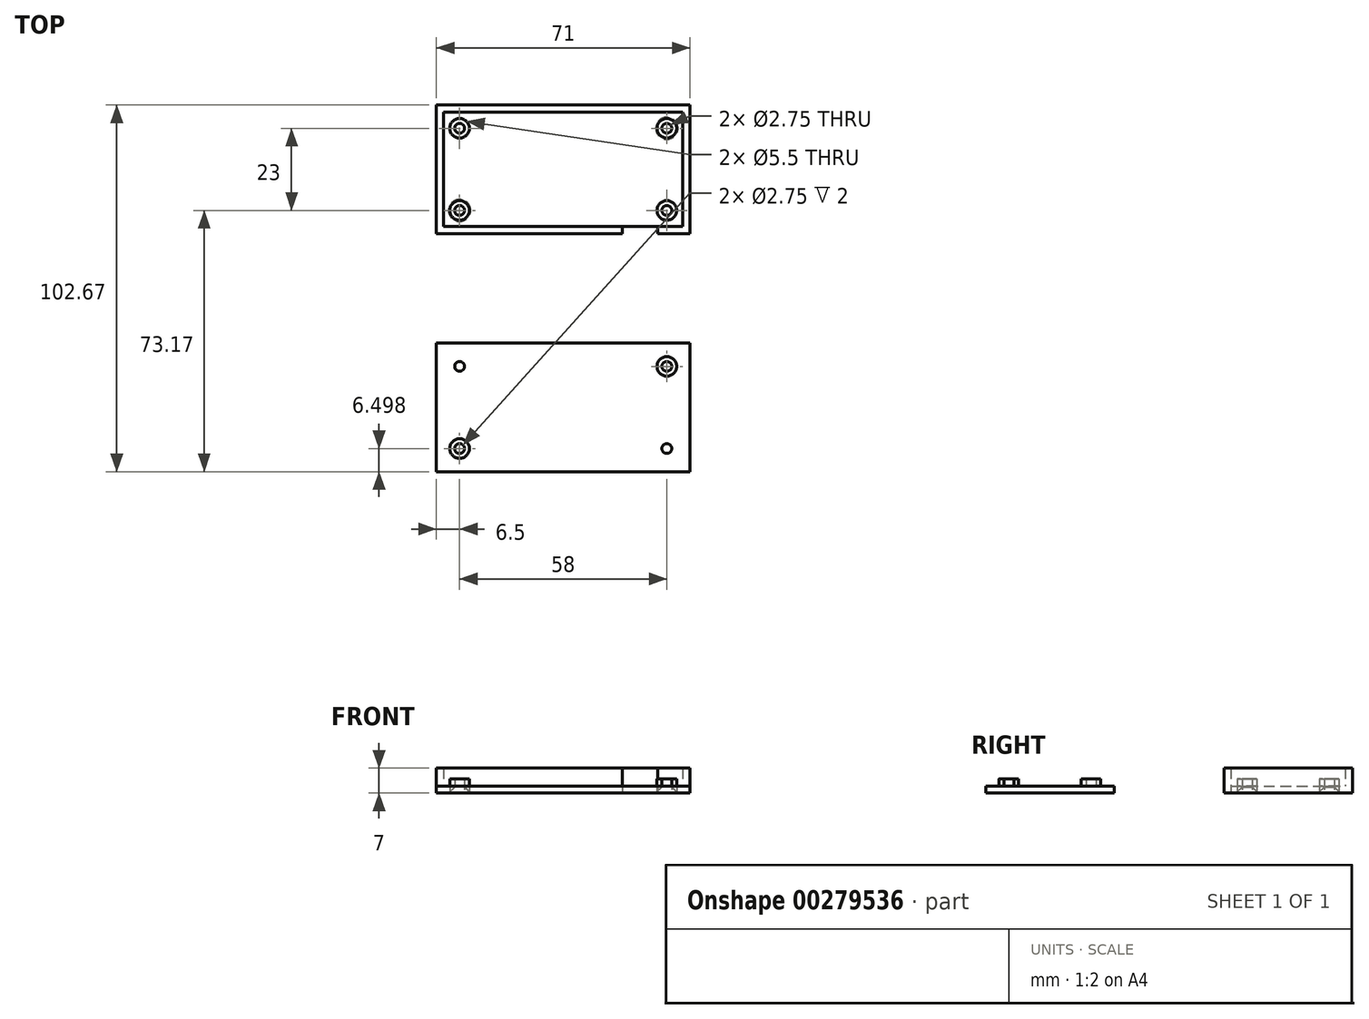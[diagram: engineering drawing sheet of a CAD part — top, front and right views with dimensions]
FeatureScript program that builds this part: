
annotation { "Feature Type Name" : "Feature", "Feature Type Description" : "" }
export const myFeature = defineFeature(function(context is Context, id is Id, definition is map)
    precondition{}
    {
        {
            var Q0;
            Q0=qCreatedBy(makeId("Top.planeOp"),FACE);
            var sketch = newSketch(context, id + "F0", { "sketchPlane" : qUnion([Q0])});
            skLineSegment(sketch, "E0.bottom", {"start": v(32.5, 15) * mm, "end": v(-32.5, 15) * mm});
            skLineSegment(sketch, "E0.top", {"start": v(32.5, -15) * mm, "end": v(-32.5, -15) * mm});
            skLineSegment(sketch, "E0.left", {"start": v(32.5, 15) * mm, "end": v(32.5, -15) * mm});
            skLineSegment(sketch, "E0.right", {"start": v(-32.5, 15) * mm, "end": v(-32.5, -15) * mm});
            skPoint(sketch, "E0.middle", {"position": v(0, 0) * mm});
            skCircle(sketch, "E1", {"center": v(29, 11.5) * mm, "radius": 1.38 * mm});
            skLineSegment(sketch, "E2", {"start": v(29, 15) * mm, "end": v(29, 11.5) * mm, "construction": true});
            skLineSegment(sketch, "E3", {"start": v(29, 11.5) * mm, "end": v(32.5, 11.5) * mm, "construction": true});
            skCircle(sketch, "E4.MirrorC", {"center": v(29, -11.5) * mm, "radius": 1.38 * mm});
            skCircle(sketch, "E5.MirrorC", {"center": v(-29, -11.5) * mm, "radius": 1.38 * mm});
            skCircle(sketch, "E6.MirrorC", {"center": v(-29, 11.5) * mm, "radius": 1.38 * mm});
            skLineSegment(sketch, "E7.0", {"start": v(33.5, 16) * mm, "end": v(-33.5, 16) * mm});
            skLineSegment(sketch, "E7.1", {"start": v(33.5, 16) * mm, "end": v(33.5, -16) * mm});
            skLineSegment(sketch, "E7.2", {"start": v(33.5, -16) * mm, "end": v(-33.5, -16) * mm});
            skLineSegment(sketch, "E7.3", {"start": v(-33.5, 16) * mm, "end": v(-33.5, -16) * mm});
            skLineSegment(sketch, "E8.0", {"start": v(35.5, 18) * mm, "end": v(-35.5, 18) * mm});
            skLineSegment(sketch, "E8.1", {"start": v(35.5, 18) * mm, "end": v(35.5, -18) * mm});
            skLineSegment(sketch, "E8.2", {"start": v(35.5, -18) * mm, "end": v(-35.5, -18) * mm});
            skLineSegment(sketch, "E8.3", {"start": v(-35.5, 18) * mm, "end": v(-35.5, -18) * mm});
            skLineSegment(sketch, "E9", {"start": v(-32.5, -15) * mm, "end": v(21.5, -15) * mm});
            skLineSegment(sketch, "E10.bottom", {"start": v(16.5, -15) * mm, "end": v(26.5, -15) * mm});
            skLineSegment(sketch, "E10.top", {"start": v(16.5, -18) * mm, "end": v(26.5, -18) * mm});
            skLineSegment(sketch, "E10.left", {"start": v(16.5, -15) * mm, "end": v(16.5, -18) * mm});
            skLineSegment(sketch, "E10.right", {"start": v(26.5, -15) * mm, "end": v(26.5, -18) * mm});
            skCircle(sketch, "E11", {"center": v(29, 11.5) * mm, "radius": 2.75 * mm});
            skCircle(sketch, "E12.MirrorC", {"center": v(29, -11.5) * mm, "radius": 2.75 * mm});
            skCircle(sketch, "E13.MirrorC", {"center": v(-29, -11.5) * mm, "radius": 2.75 * mm});
            skCircle(sketch, "E14.MirrorC", {"center": v(-29, 11.5) * mm, "radius": 2.75 * mm});
            skSolve(sketch);
        }
        {
            var Q0;
            Q0=makeQuery(id+"F0.imprint","IMPRINT",FACE,{"disambiguationData":[TD([[makeQuery(id+"F0.imprint","IMPRINT",EDGE,{"derivedFrom":sQuery(id+"F0.wireOp",EDGE,"E7.0")}),-1.0]])]});
            var Q1;
            Q1=makeQuery(id+"F0.imprint","IMPRINT",FACE,{"disambiguationData":[TD([[makeQuery(id+"F0.imprint","IMPRINT",EDGE,{"derivedFrom":sQuery(id+"F0.wireOp",EDGE,"E0.bottom")}),-1.0]])]});
            var Q2;
            Q2=makeQuery(id+"F0.imprint","IMPRINT",FACE,{"disambiguationData":[TD([[makeQuery(id+"F0.imprint","IMPRINT",EDGE,{"derivedFrom":sQuery(id+"F0.wireOp",EDGE,"E0.bottom")}),1.0]])]});
            var Q3;
            Q3=makeQuery(id+"F0.imprint","IMPRINT",FACE,{"disambiguationData":[TD([[makeQuery(id+"F0.imprint","IMPRINT",EDGE,{"derivedFrom":sQuery(id+"F0.wireOp",EDGE,"E6.MirrorC")}),1.0]])]});
            var Q4;
            Q4=makeQuery(id+"F0.imprint","IMPRINT",FACE,{"disambiguationData":[TD([[makeQuery(id+"F0.imprint","IMPRINT",EDGE,{"derivedFrom":sQuery(id+"F0.wireOp",EDGE,"E5.MirrorC")}),-1.0]])]});
            var Q5;
            Q5=makeQuery(id+"F0.imprint","IMPRINT",FACE,{"disambiguationData":[TD([[makeQuery(id+"F0.imprint","IMPRINT",EDGE,{"derivedFrom":sQuery(id+"F0.wireOp",EDGE,"E1")}),-1.0]])]});
            var Q6;
            Q6=makeQuery(id+"F0.imprint","IMPRINT",FACE,{"disambiguationData":[TD([[makeQuery(id+"F0.imprint","IMPRINT",EDGE,{"derivedFrom":sQuery(id+"F0.wireOp",EDGE,"E4.MirrorC")}),1.0]])]});
            var Q7;
            {var subQ5=sQuery(id+"F0.wireOp",EDGE,"E10.top");Q7=makeQuery(id+"F0.imprint","IMPRINT",FACE,{"disambiguationData":[TD([[makeQuery(id+"F0.imprint","IMPRINT",EDGE,{"derivedFrom":subQ5}),1.0]])]});}
            var Q8;
            {var subQ3=sQuery(id+"F0.wireOp",EDGE,"E7.2");var subQ5=sQuery(id+"F0.wireOp",EDGE,"E10.right");var subQ8=makeQuery(id+"F0.imprint","INTERSECT",VERTEX,{"derivedFrom":[subQ3,subQ5]});Q8=makeQuery(id+"F0.imprint","IMPRINT",FACE,{"disambiguationData":[TD([[makeQuery(id+"F0.imprint","IMPRINT",EDGE,{"disambiguationData":[TD([[subQ8,-1.0]])],"derivedFrom":subQ3}),-1.0]])]});}
            extrude(context, id + "F1", {"entities" : qUnion([Q0, Q1, Q2, Q3, Q4, Q5, Q6, Q7, Q8]), "depth" : 2 * mm});
        }
        {
            var Q0;
            Q0=makeQuery(id+"F0.imprint","IMPRINT",FACE,{"disambiguationData":[TD([[makeQuery(id+"F0.imprint","IMPRINT",EDGE,{"derivedFrom":sQuery(id+"F0.wireOp",EDGE,"E5.MirrorC")}),-1.0]])]});
            var Q1;
            Q1=makeQuery(id+"F0.imprint","IMPRINT",FACE,{"disambiguationData":[TD([[makeQuery(id+"F0.imprint","IMPRINT",EDGE,{"derivedFrom":sQuery(id+"F0.wireOp",EDGE,"E4.MirrorC")}),1.0]])]});
            var Q2;
            Q2=makeQuery(id+"F0.imprint","IMPRINT",FACE,{"disambiguationData":[TD([[makeQuery(id+"F0.imprint","IMPRINT",EDGE,{"derivedFrom":sQuery(id+"F0.wireOp",EDGE,"E1")}),-1.0]])]});
            var Q3;
            Q3=makeQuery(id+"F0.imprint","IMPRINT",FACE,{"disambiguationData":[TD([[makeQuery(id+"F0.imprint","IMPRINT",EDGE,{"derivedFrom":sQuery(id+"F0.wireOp",EDGE,"E6.MirrorC")}),1.0]])]});
            extrude(context, id + "F2", {"entities" : qUnion([Q0, Q1, Q2, Q3]), "operationType" : NewBodyOperationType.ADD, "depth" : 4 * mm});
        }
        {
            var Q0;
            Q0=makeQuery(id+"F0.imprint","IMPRINT",FACE,{"disambiguationData":[TD([[makeQuery(id+"F0.imprint","IMPRINT",EDGE,{"derivedFrom":sQuery(id+"F0.wireOp",EDGE,"E7.0")}),-1.0]])]});
            extrude(context, id + "F3", {"entities" : qUnion([Q0]), "operationType" : NewBodyOperationType.ADD, "depth" : 7 * mm});
        }
        {
            var Q0;
            Q0=makeQuery(id+"F1.opExtrude","CAP_EDGE",EDGE,{"disambiguationData":[OSD([sQuery(id+"F0.wireOp",EDGE,"E4.MirrorC")])],"isStart":true});
            var Q1;
            Q1=makeQuery(id+"F1.opExtrude","CAP_EDGE",EDGE,{"disambiguationData":[OSD([sQuery(id+"F0.wireOp",EDGE,"E1")])],"isStart":true});
            var Q2;
            Q2=makeQuery(id+"F1.opExtrude","CAP_EDGE",EDGE,{"disambiguationData":[OSD([sQuery(id+"F0.wireOp",EDGE,"E6.MirrorC")])],"isStart":true});
            var Q3;
            Q3=makeQuery(id+"F1.opExtrude","CAP_EDGE",EDGE,{"disambiguationData":[OSD([sQuery(id+"F0.wireOp",EDGE,"E5.MirrorC")])],"isStart":true});
            chamfer(context, id + "F4", {"entities" : qUnion([Q0, Q1, Q2, Q3]), "width" : 1.75 * mm, "tangentPropagation" : true});
        }
        {
            var Q0;
            Q0=qCreatedBy(makeId("Top.planeOp"),FACE);
            var sketch = newSketch(context, id + "F5", { "sketchPlane" : qUnion([Q0])});
            skLineSegment(sketch, "E15.bottom", {"start": v(35.5, -48.67) * mm, "end": v(-35.5, -48.67) * mm});
            skLineSegment(sketch, "E15.top", {"start": v(35.5, -84.67) * mm, "end": v(-35.5, -84.67) * mm});
            skLineSegment(sketch, "E15.left", {"start": v(35.5, -48.67) * mm, "end": v(35.5, -84.67) * mm});
            skLineSegment(sketch, "E15.right", {"start": v(-35.5, -48.67) * mm, "end": v(-35.5, -84.67) * mm});
            skPoint(sketch, "E15.middle", {"position": v(0, -66.67) * mm});
            skLineSegment(sketch, "E16", {"start": v(29, -48.67) * mm, "end": v(29, -55.17) * mm, "construction": true});
            skLineSegment(sketch, "E17", {"start": v(29, -55.17) * mm, "end": v(35.5, -55.17) * mm, "construction": true});
            skCircle(sketch, "E18", {"center": v(29, -55.17) * mm, "radius": 1.38 * mm});
            skCircle(sketch, "E19", {"center": v(29, -55.17) * mm, "radius": 2.75 * mm});
            skCircle(sketch, "E20.MirrorC", {"center": v(-29, -55.17) * mm, "radius": 1.38 * mm});
            skCircle(sketch, "E21.MirrorC", {"center": v(-29, -55.17) * mm, "radius": 2.75 * mm});
            skLineSegment(sketch, "E22", {"start": v(0, -66.67) * mm, "end": v(-17.15, -66.67) * mm});
            skCircle(sketch, "E23.MirrorC", {"center": v(29, -78.17) * mm, "radius": 1.38 * mm});
            skCircle(sketch, "E24.MirrorC", {"center": v(29, -78.17) * mm, "radius": 2.75 * mm});
            skCircle(sketch, "E25.MirrorC", {"center": v(-29, -78.17) * mm, "radius": 1.38 * mm});
            skCircle(sketch, "E26.MirrorC", {"center": v(-29, -78.17) * mm, "radius": 2.75 * mm});
            skSolve(sketch);
        }
        {
            var Q0;
            Q0=makeQuery(id+"F5.imprint","IMPRINT",FACE,{"disambiguationData":[TD([[makeQuery(id+"F5.imprint","IMPRINT",EDGE,{"derivedFrom":sQuery(id+"F5.wireOp",EDGE,"E15.bottom")}),1.0]])]});
            var Q1;
            Q1=makeQuery(id+"F5.imprint","IMPRINT",FACE,{"disambiguationData":[TD([[makeQuery(id+"F5.imprint","IMPRINT",EDGE,{"derivedFrom":sQuery(id+"F5.wireOp",EDGE,"E20.MirrorC")}),1.0]])]});
            var Q2;
            Q2=makeQuery(id+"F5.imprint","IMPRINT",FACE,{"disambiguationData":[TD([[makeQuery(id+"F5.imprint","IMPRINT",EDGE,{"derivedFrom":sQuery(id+"F5.wireOp",EDGE,"E20.MirrorC")}),-1.0]])]});
            var Q3;
            Q3=makeQuery(id+"F5.imprint","IMPRINT",FACE,{"disambiguationData":[TD([[makeQuery(id+"F5.imprint","IMPRINT",EDGE,{"derivedFrom":sQuery(id+"F5.wireOp",EDGE,"E25.MirrorC")}),1.0]])]});
            var Q4;
            Q4=makeQuery(id+"F5.imprint","IMPRINT",FACE,{"disambiguationData":[TD([[makeQuery(id+"F5.imprint","IMPRINT",EDGE,{"derivedFrom":sQuery(id+"F5.wireOp",EDGE,"E25.MirrorC")}),-1.0]])]});
            var Q5;
            Q5=makeQuery(id+"F5.imprint","IMPRINT",FACE,{"disambiguationData":[TD([[makeQuery(id+"F5.imprint","IMPRINT",EDGE,{"derivedFrom":sQuery(id+"F5.wireOp",EDGE,"E23.MirrorC")}),1.0]])]});
            var Q6;
            Q6=makeQuery(id+"F5.imprint","IMPRINT",FACE,{"disambiguationData":[TD([[makeQuery(id+"F5.imprint","IMPRINT",EDGE,{"derivedFrom":sQuery(id+"F5.wireOp",EDGE,"E23.MirrorC")}),-1.0]])]});
            var Q7;
            Q7=makeQuery(id+"F5.imprint","IMPRINT",FACE,{"disambiguationData":[TD([[makeQuery(id+"F5.imprint","IMPRINT",EDGE,{"derivedFrom":sQuery(id+"F5.wireOp",EDGE,"E18")}),-1.0]])]});
            var Q8;
            Q8=makeQuery(id+"F5.imprint","IMPRINT",FACE,{"disambiguationData":[TD([[makeQuery(id+"F5.imprint","IMPRINT",EDGE,{"derivedFrom":sQuery(id+"F5.wireOp",EDGE,"E18")}),1.0]])]});
            extrude(context, id + "F6", {"entities" : qUnion([Q0, Q1, Q2, Q3, Q4, Q5, Q6, Q7, Q8]), "depth" : 2 * mm});
        }
        {
            var Q0;
            Q0=makeQuery(id+"F5.imprint","IMPRINT",FACE,{"disambiguationData":[TD([[makeQuery(id+"F5.imprint","IMPRINT",EDGE,{"derivedFrom":sQuery(id+"F5.wireOp",EDGE,"E25.MirrorC")}),-1.0]])]});
            var Q1;
            Q1=makeQuery(id+"F5.imprint","IMPRINT",FACE,{"disambiguationData":[TD([[makeQuery(id+"F5.imprint","IMPRINT",EDGE,{"derivedFrom":sQuery(id+"F5.wireOp",EDGE,"E20.MirrorC")}),1.0]])]});
            var Q2;
            Q2=makeQuery(id+"F5.imprint","IMPRINT",FACE,{"disambiguationData":[TD([[makeQuery(id+"F5.imprint","IMPRINT",EDGE,{"derivedFrom":sQuery(id+"F5.wireOp",EDGE,"E23.MirrorC")}),1.0]])]});
            var Q3;
            Q3=makeQuery(id+"F5.imprint","IMPRINT",FACE,{"disambiguationData":[TD([[makeQuery(id+"F5.imprint","IMPRINT",EDGE,{"derivedFrom":sQuery(id+"F5.wireOp",EDGE,"E18")}),-1.0]])]});
            extrude(context, id + "F7", {"entities" : qUnion([Q0, Q1, Q2, Q3]), "operationType" : NewBodyOperationType.ADD, "depth" : 4 * mm});
        }
    });
